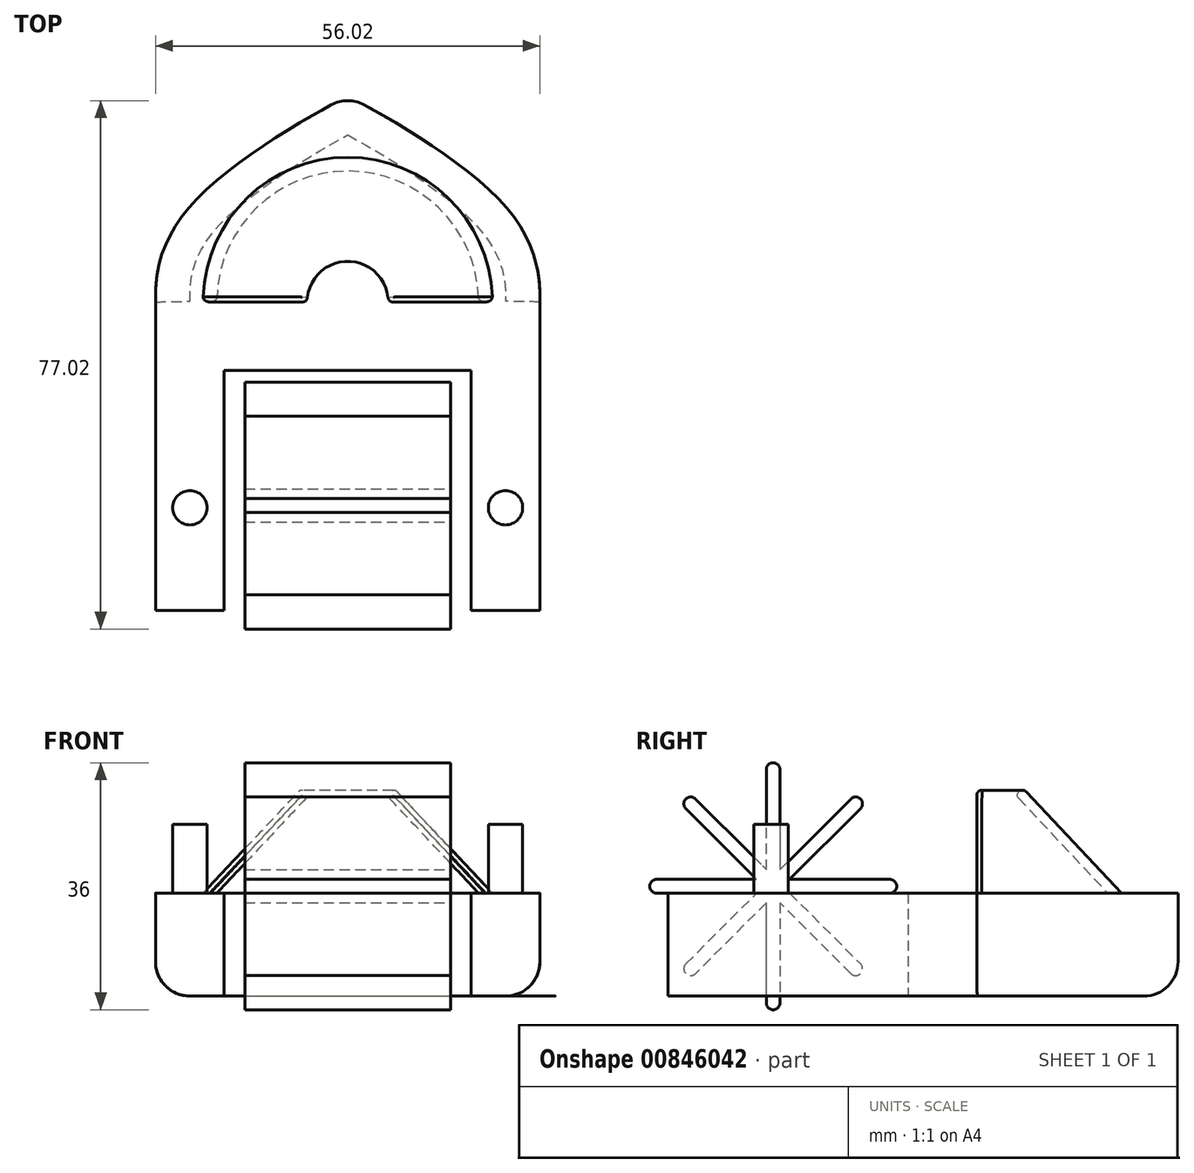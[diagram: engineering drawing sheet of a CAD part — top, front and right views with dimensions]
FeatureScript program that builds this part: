
annotation { "Feature Type Name" : "Feature", "Feature Type Description" : "" }
export const myFeature = defineFeature(function(context is Context, id is Id, definition is map)
    precondition{}
    {
        {
            var Q0;
            Q0=qCreatedBy(makeId("Top.planeOp"),FACE);
            var sketch = newSketch(context, id + "F0", { "sketchPlane" : qUnion([Q0])});
            skLineSegment(sketch, "E0", {"start": v(-28, 0) * mm, "end": v(-28, -45) * mm});
            skLineSegment(sketch, "E1", {"start": v(-28, -45) * mm, "end": v(-18, -45) * mm});
            skLineSegment(sketch, "E2", {"start": v(-18, -45) * mm, "end": v(-18, -10) * mm});
            skFitSpline(sketch, "E3", {"points": [v(0, 30) * mm, v(-22, 15) * mm, v(-28, 0) * mm], "startDerivative": vector(-24, -12.35) * mm, "endDerivative": vector(1.2, -35.8) * mm});
            skLineSegment(sketch, "E4.MirrorCS", {"start": v(28, -45) * mm, "end": v(18, -45) * mm});
            skLineSegment(sketch, "E5.MirrorCS", {"start": v(18, -45) * mm, "end": v(18, -10) * mm});
            skLineSegment(sketch, "E6.MirrorCS", {"start": v(28, 0) * mm, "end": v(28, -45) * mm});
            skFitSpline(sketch, "E7.MirrorCS", {"points": [v(0, 30) * mm, v(22, 15) * mm, v(28, 0) * mm], "startDerivative": vector(24, -12.35) * mm, "endDerivative": vector(-1.2, -35.8) * mm});
            skLineSegment(sketch, "E8", {"start": v(-18, -10) * mm, "end": v(18, -10) * mm});
            skSolve(sketch);
        }
        {
            var Q0;
            Q0 = qSketchRegion(id + "F0", true);
            extrude(context, id + "F1", {"entities" : qUnion([Q0]), "depth" : 15 * mm, "offsetDistance" : 25 * mm});
        }
        {
            var Q0;
            Q0=makeQuery(id+"F1.opExtrude","CAP_EDGE",EDGE,{"disambiguationData":[OSD([sQuery(id+"F0.wireOp",EDGE,"E7.MirrorCS")])],"isStart":true});
            var Q1;
            Q1=makeQuery(id+"F1.opExtrude","CAP_EDGE",EDGE,{"disambiguationData":[OSD([sQuery(id+"F0.wireOp",EDGE,"E3")])],"isStart":true});
            var Q2;
            Q2=makeQuery(id+"F1.opExtrude","SWEPT_EDGE",EDGE,{"disambiguationData":[OSD([sQuery(id+"F0.wireOp",EDGE,"E3"),sQuery(id+"F0.wireOp",EDGE,"E7.MirrorCS")])]});
            fillet(context, id + "F2", {"entities" : qUnion([Q0, Q1, Q2]), "radius" : 5 * mm, "tangentPropagation" : true, "allowEdgeOverflow" : false});
        }
        {
            var Q0;
            Q0=makeQuery(id+"F1.opExtrude","CAP_FACE",FACE,{"disambiguationData":[OSD([sQuery(id+"F0.wireOp",EDGE,"E0"),sQuery(id+"F0.wireOp",EDGE,"E1"),sQuery(id+"F0.wireOp",EDGE,"E2"),sQuery(id+"F0.wireOp",EDGE,"E3"),sQuery(id+"F0.wireOp",EDGE,"E4.MirrorCS"),sQuery(id+"F0.wireOp",EDGE,"E5.MirrorCS"),sQuery(id+"F0.wireOp",EDGE,"E6.MirrorCS"),sQuery(id+"F0.wireOp",EDGE,"E7.MirrorCS"),sQuery(id+"F0.wireOp",EDGE,"E8")])],"isStart":false});
            var sketch = newSketch(context, id + "F3", { "sketchPlane" : qUnion([Q0])});
            skCircle(sketch, "E9", {"center": v(-23, -30) * mm, "radius": 2.5 * mm});
            skLineSegment(sketch, "E10", {"start": v(-30.83, -30) * mm, "end": v(42.3, -30) * mm, "construction": true});
            skCircle(sketch, "E11.MirrorC", {"center": v(23, -30) * mm, "radius": 2.5 * mm});
            skSolve(sketch);
        }
        {
            var Q0;
            Q0 = qSketchRegion(id + "F3", true);
            extrude(context, id + "F4", {"entities" : qUnion([Q0]), "operationType" : NewBodyOperationType.ADD, "depth" : 10 * mm, "offsetDistance" : 25 * mm});
        }
        {
            var Q0;
            Q0=qCreatedBy(makeId("Right.planeOp"),FACE);
            var sketch = newSketch(context, id + "F5", { "sketchPlane" : qUnion([Q0])});
            skLineSegment(sketch, "E12", {"start": v(20, 14.02) * mm, "end": v(22, 14.02) * mm});
            skLineSegment(sketch, "E13", {"start": v(22, 14.02) * mm, "end": v(7, 30) * mm});
            skLineSegment(sketch, "E14", {"start": v(5, 30) * mm, "end": v(20, 14.02) * mm});
            skLineSegment(sketch, "E15", {"start": v(5, 30) * mm, "end": v(7, 30) * mm});
            skLineSegment(sketch, "E16", {"start": v(0, 30) * mm, "end": v(0, 15.09) * mm, "construction": true});
            skSolve(sketch);
        }
        {
            var Q0;
            Q0 = qSketchRegion(id + "F5", true);
            var Q1;
            Q1=sQuery(id+"F5.wireOp",EDGE,"E16");
            revolve(context, id + "F6", {"operationType" : NewBodyOperationType.ADD, "surfaceOperationType" : NewSurfaceOperationType.NEW, "entities" : qUnion([Q0]), "axis" : qUnion([Q1]), "revolveType" : RevolveType.SYMMETRIC, "angle" : 180 * degree});
        }
        {
            var Q0;
            Q0=makeQuery(id+"F6.opRevolve","SWEPT_EDGE",EDGE,{"disambiguationData":[OSD([sQuery(id+"F5.wireOp",EDGE,"E13"),sQuery(id+"F5.wireOp",EDGE,"E15")])]});
            var Q1;
            Q1=makeQuery(id+"F6.opRevolve","SWEPT_EDGE",EDGE,{"disambiguationData":[OSD([sQuery(id+"F5.wireOp",EDGE,"E14"),sQuery(id+"F5.wireOp",EDGE,"E15")])]});
            var Q2;
            Q2=makeQuery(id+"F6.opRevolve","CAP_EDGE",EDGE,{"disambiguationData":[OSD([sQuery(id+"F5.wireOp",EDGE,"E13")])],"isStart":true});
            var Q3;
            Q3=makeQuery(id+"F6.opRevolve","CAP_EDGE",EDGE,{"disambiguationData":[OSD([sQuery(id+"F5.wireOp",EDGE,"E14")])],"isStart":true});
            var Q4;
            Q4=makeQuery(id+"F6.opRevolve","CAP_EDGE",EDGE,{"disambiguationData":[OSD([sQuery(id+"F5.wireOp",EDGE,"E15")])],"isStart":true});
            var Q5;
            Q5=makeQuery(id+"F6.opRevolve","CAP_EDGE",EDGE,{"disambiguationData":[OSD([sQuery(id+"F5.wireOp",EDGE,"E15")])],"isStart":false});
            var Q6;
            Q6=makeQuery(id+"F6.opRevolve","CAP_EDGE",EDGE,{"disambiguationData":[OSD([sQuery(id+"F5.wireOp",EDGE,"E14")])],"isStart":false});
            var Q7;
            Q7=makeQuery(id+"F6.opRevolve","CAP_EDGE",EDGE,{"disambiguationData":[OSD([sQuery(id+"F5.wireOp",EDGE,"E13")])],"isStart":false});
            fillet(context, id + "F7", {"entities" : qUnion([Q0, Q1, Q2, Q3, Q4, Q5, Q6, Q7]), "radius" : .7 * mm, "tangentPropagation" : true, "allowEdgeOverflow" : false});
        }
        {
            var Q0;
            Q0=qCreatedBy(makeId("Right.planeOp"),FACE);
            cPlane(context, id + "F8", {"entities" : qUnion([Q0]), "cplaneType" : CPlaneType.OFFSET, "offset" : 0 * mm, "width" : 150 * mm, "height" : 150 * mm});
        }
        {
            var Q0;
            Q0=qCreatedBy(id+"F8.planeOp",FACE);
            var sketch = newSketch(context, id + "F9", { "sketchPlane" : qUnion([Q0])});
            skLineSegment(sketch, "E17", {"start": v(-30.68, 16) * mm, "end": v(-30.68, 33) * mm});
            skLineSegment(sketch, "E18", {"start": v(-29.68, 34) * mm, "end": v(-29.68, 34) * mm});
            skLineSegment(sketch, "E19", {"start": v(-28.68, 33) * mm, "end": v(-28.68, 16) * mm});
            skLineSegment(sketch, "E20", {"start": v(-28.68, 16) * mm, "end": v(-30.68, 16) * mm});
            skLineSegment(sketch, "E21", {"start": v(-30.68, 16) * mm, "end": v(-28.68, 16) * mm});
            skPoint(sketch, "E22.visualSharp", {"position": v(-30.68, 34) * mm});
            skArc(sketch, "E22.filletArc", {"start": v(-29.68, 34) * mm, "mid": v(-30.38, 33.7) * mm, "end": v(-30.68, 33) * mm});
            skPoint(sketch, "E23.visualSharp", {"position": v(-28.68, 34) * mm});
            skArc(sketch, "E23.filletArc", {"start": v(-28.68, 33) * mm, "mid": v(-28.97, 33.7) * mm, "end": v(-29.68, 34) * mm});
            skLineSegment(sketch, "E24.1.0", {"start": v(-30.38, 15.3) * mm, "end": v(-42.4, 27.31) * mm});
            skPoint(sketch, "E24.1.1", {"position": v(-43.11, 28.02) * mm});
            skLineSegment(sketch, "E24.1.2", {"start": v(-30.38, 15.3) * mm, "end": v(-28.97, 16.7) * mm});
            skLineSegment(sketch, "E24.1.3", {"start": v(-41, 28.73) * mm, "end": v(-28.97, 16.7) * mm});
            skPoint(sketch, "E24.1.4", {"position": v(-41.7, 29.44) * mm});
            skArc(sketch, "E24.1.5", {"start": v(-42.4, 28.73) * mm, "mid": v(-42.7, 28.02) * mm, "end": v(-42.4, 27.31) * mm});
            skLineSegment(sketch, "E24.1.6", {"start": v(-28.97, 16.7) * mm, "end": v(-30.38, 15.3) * mm});
            skArc(sketch, "E24.1.7", {"start": v(-41, 28.73) * mm, "mid": v(-41.7, 29.02) * mm, "end": v(-42.4, 28.73) * mm});
            skLineSegment(sketch, "E24.2.0", {"start": v(-29.68, 15) * mm, "end": v(-46.68, 15) * mm});
            skPoint(sketch, "E24.2.1", {"position": v(-47.68, 15) * mm});
            skLineSegment(sketch, "E24.2.2", {"start": v(-29.68, 15) * mm, "end": v(-29.68, 17) * mm});
            skLineSegment(sketch, "E24.2.3", {"start": v(-46.68, 17) * mm, "end": v(-29.68, 17) * mm});
            skPoint(sketch, "E24.2.4", {"position": v(-47.68, 17) * mm});
            skArc(sketch, "E24.2.5", {"start": v(-47.68, 16) * mm, "mid": v(-47.38, 15.3) * mm, "end": v(-46.68, 15) * mm});
            skLineSegment(sketch, "E24.2.6", {"start": v(-29.68, 17) * mm, "end": v(-29.68, 15) * mm});
            skArc(sketch, "E24.2.7", {"start": v(-46.68, 17) * mm, "mid": v(-47.38, 16.7) * mm, "end": v(-47.68, 16) * mm});
            skLineSegment(sketch, "E24.3.0", {"start": v(-28.97, 15.3) * mm, "end": v(-41, 3.27) * mm});
            skPoint(sketch, "E24.3.1", {"position": v(-41.7, 2.56) * mm});
            skLineSegment(sketch, "E24.3.2", {"start": v(-28.97, 15.3) * mm, "end": v(-30.38, 16.7) * mm});
            skLineSegment(sketch, "E24.3.3", {"start": v(-42.4, 4.69) * mm, "end": v(-30.38, 16.7) * mm});
            skPoint(sketch, "E24.3.4", {"position": v(-43.11, 3.98) * mm});
            skArc(sketch, "E24.3.5", {"start": v(-42.4, 3.27) * mm, "mid": v(-41.7, 2.98) * mm, "end": v(-41, 3.27) * mm});
            skLineSegment(sketch, "E24.3.6", {"start": v(-30.38, 16.7) * mm, "end": v(-28.97, 15.3) * mm});
            skArc(sketch, "E24.3.7", {"start": v(-42.4, 4.69) * mm, "mid": v(-42.7, 3.98) * mm, "end": v(-42.4, 3.27) * mm});
            skLineSegment(sketch, "E24.4.0", {"start": v(-28.68, 16) * mm, "end": v(-28.68, -1) * mm});
            skPoint(sketch, "E24.4.1", {"position": v(-28.68, -2) * mm});
            skLineSegment(sketch, "E24.4.3", {"start": v(-30.68, -1) * mm, "end": v(-30.68, 16) * mm});
            skPoint(sketch, "E24.4.4", {"position": v(-30.68, -2) * mm});
            skArc(sketch, "E24.4.5", {"start": v(-29.68, -2) * mm, "mid": v(-28.97, -1.7) * mm, "end": v(-28.68, -1) * mm});
            skArc(sketch, "E24.4.7", {"start": v(-30.68, -1) * mm, "mid": v(-30.38, -1.7) * mm, "end": v(-29.68, -2) * mm});
            skLineSegment(sketch, "E24.5.0", {"start": v(-28.97, 16.7) * mm, "end": v(-16.95, 4.69) * mm});
            skPoint(sketch, "E24.5.1", {"position": v(-16.24, 3.98) * mm});
            skLineSegment(sketch, "E24.5.2", {"start": v(-28.97, 16.7) * mm, "end": v(-30.38, 15.3) * mm});
            skLineSegment(sketch, "E24.5.3", {"start": v(-18.36, 3.27) * mm, "end": v(-30.38, 15.3) * mm});
            skPoint(sketch, "E24.5.4", {"position": v(-17.66, 2.56) * mm});
            skArc(sketch, "E24.5.5", {"start": v(-16.95, 3.27) * mm, "mid": v(-16.66, 3.98) * mm, "end": v(-16.95, 4.69) * mm});
            skLineSegment(sketch, "E24.5.6", {"start": v(-30.38, 15.3) * mm, "end": v(-28.97, 16.7) * mm});
            skArc(sketch, "E24.5.7", {"start": v(-18.36, 3.27) * mm, "mid": v(-17.66, 2.98) * mm, "end": v(-16.95, 3.27) * mm});
            skLineSegment(sketch, "E24.6.0", {"start": v(-29.68, 17) * mm, "end": v(-12.68, 17) * mm});
            skPoint(sketch, "E24.6.1", {"position": v(-11.68, 17) * mm});
            skLineSegment(sketch, "E24.6.2", {"start": v(-29.68, 17) * mm, "end": v(-29.68, 15) * mm});
            skLineSegment(sketch, "E24.6.3", {"start": v(-12.68, 15) * mm, "end": v(-29.68, 15) * mm});
            skPoint(sketch, "E24.6.4", {"position": v(-11.68, 15) * mm});
            skArc(sketch, "E24.6.5", {"start": v(-11.68, 16) * mm, "mid": v(-11.97, 16.7) * mm, "end": v(-12.68, 17) * mm});
            skLineSegment(sketch, "E24.6.6", {"start": v(-29.68, 15) * mm, "end": v(-29.68, 17) * mm});
            skArc(sketch, "E24.6.7", {"start": v(-12.68, 15) * mm, "mid": v(-11.97, 15.3) * mm, "end": v(-11.68, 16) * mm});
            skLineSegment(sketch, "E24.7.0", {"start": v(-30.38, 16.7) * mm, "end": v(-18.36, 28.73) * mm});
            skPoint(sketch, "E24.7.1", {"position": v(-17.66, 29.44) * mm});
            skLineSegment(sketch, "E24.7.2", {"start": v(-30.38, 16.7) * mm, "end": v(-28.97, 15.3) * mm});
            skLineSegment(sketch, "E24.7.3", {"start": v(-16.95, 27.31) * mm, "end": v(-28.97, 15.3) * mm});
            skPoint(sketch, "E24.7.4", {"position": v(-16.24, 28.02) * mm});
            skArc(sketch, "E24.7.5", {"start": v(-16.95, 28.73) * mm, "mid": v(-17.66, 29.02) * mm, "end": v(-18.36, 28.73) * mm});
            skLineSegment(sketch, "E24.7.6", {"start": v(-28.97, 15.3) * mm, "end": v(-30.38, 16.7) * mm});
            skArc(sketch, "E24.7.7", {"start": v(-16.95, 27.31) * mm, "mid": v(-16.66, 28.02) * mm, "end": v(-16.95, 28.73) * mm});
            skPoint(sketch, "E24.center", {"position": v(-29.68, 16) * mm});
            skSolve(sketch);
        }
        {
            var Q0;
            Q0 = qSketchRegion(id + "F9", true);
            extrude(context, id + "F10", {"entities" : qUnion([Q0]), "endBound" : BoundingType.SYMMETRIC, "oppositeDirection" : true, "depth" : 30 * mm, "offsetDistance" : 25 * mm});
        }
        {
            var Q0;
            Q0=qCreatedBy(id+"F8.planeOp",FACE);
            var sketch = newSketch(context, id + "F11", { "sketchPlane" : qUnion([Q0])});
            skCircle(sketch, "E25", {"center": v(-29.74, 16) * mm, "radius": 1.77 * mm});
            skSolve(sketch);
        }
        {
            var Q0;
            Q0 = qSketchRegion(id + "F11", true);
            extrude(context, id + "F12", {"entities" : qUnion([Q0]), "operationType" : NewBodyOperationType.ADD, "endBound" : BoundingType.SYMMETRIC, "depth" : 30 * mm, "offsetDistance" : 25 * mm});
        }
    });
